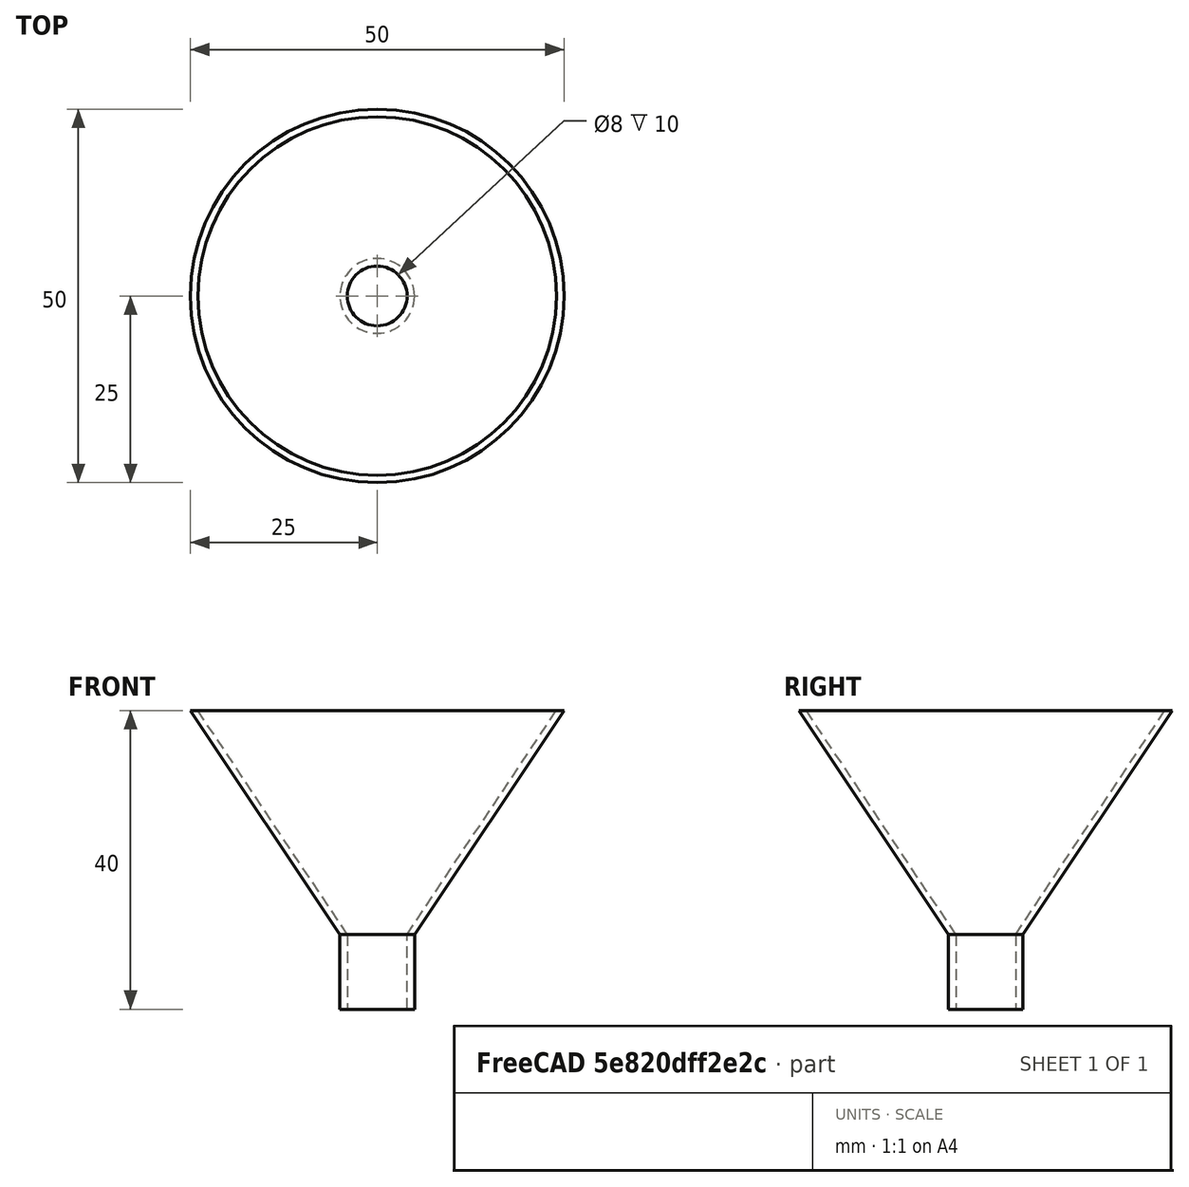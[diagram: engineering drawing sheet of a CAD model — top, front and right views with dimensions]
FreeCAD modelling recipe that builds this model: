
FCSTD DOCUMENT  (FreeCAD 1.0R39319 (Git))
Label: ojt1_t14r03_funnel
License: All rights reserved
LicenseURL: https://en.wikipedia.org/wiki/All_rights_reserved
objects: Part::Cone×2, Part::Cut×2, Part::Cylinder×2, Part::MultiFuse×1
note: 7 computed .brp shape members not serialized (recipe doc carries the construction recipe); baked Part::Feature solids carry a one-line shape summary decoded from their .brp

FEATURE [Part::Cone] Cone  label="Con"
  Angle = 360
  AttacherType = Attacher::AttachEngine3D
  Height = 30
  Radius1 = 5
  Radius2 = 25
FEATURE [Part::Cone] Cone001  label="Con001"
  Angle = 360
  AttacherType = Attacher::AttachEngine3D
  Height = 30
  Radius1 = 4
  Radius2 = 24
FEATURE [Part::Cut] Cut
  Base = -> Cone
  Tool = -> Cone001
FEATURE [Part::Cylinder] Cylinder  label="Cilindre"
  Angle = 360
  AttacherType = Attacher::AttachEngine3D
  FirstAngle = 0
  Height = 10
  Placement = pos=(0,0,-10) rot=(0,0,1;0rad)
  Radius = 5
  SecondAngle = 0
FEATURE [Part::Cylinder] Cylinder001  label="Cilindre001"
  Angle = 360
  AttacherType = Attacher::AttachEngine3D
  FirstAngle = 0
  Height = 10
  Placement = pos=(0,0,-10) rot=(0,0,1;0rad)
  Radius = 4
  SecondAngle = 0
FEATURE [Part::Cut] Cut001
  Base = -> Cylinder
  Tool = -> Cylinder001
FEATURE [Part::MultiFuse] Fusion  label="embut"
  Shapes = -> [Cut001,Cut]
